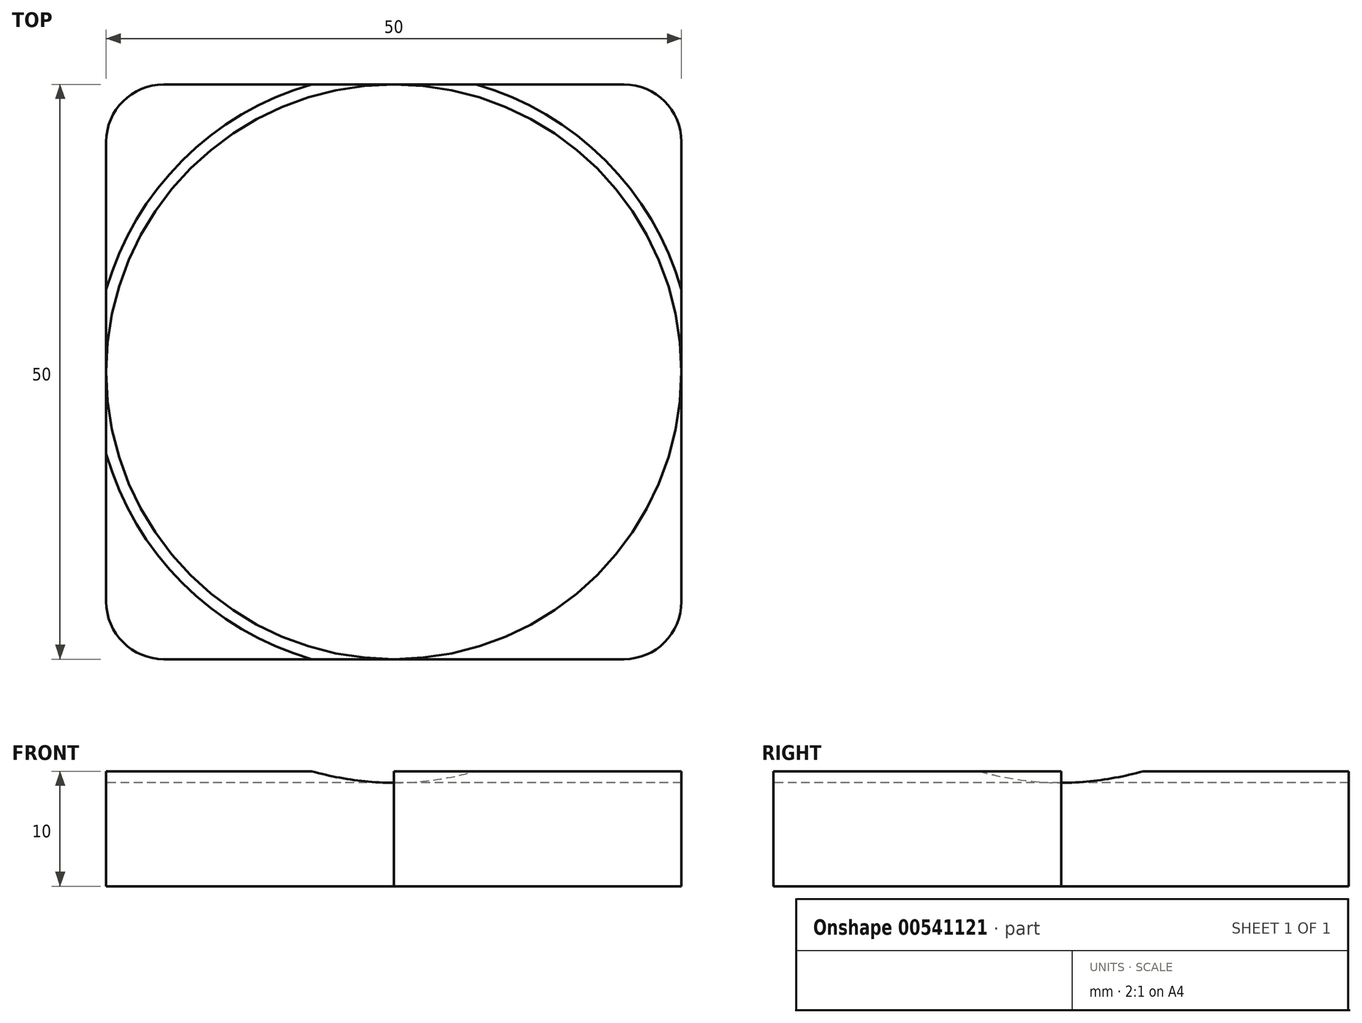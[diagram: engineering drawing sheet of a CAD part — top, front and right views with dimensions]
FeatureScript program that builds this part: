
annotation { "Feature Type Name" : "Feature", "Feature Type Description" : "" }
export const myFeature = defineFeature(function(context is Context, id is Id, definition is map)
    precondition{}
    {
        {
            var Q0;
            Q0=qCreatedBy(makeId("Top.planeOp"),FACE);
            var sketch = newSketch(context, id + "F0", { "sketchPlane" : qUnion([Q0])});
            skLineSegment(sketch, "E0.bottom", {"start": v(25, 25) * mm, "end": v(-25, 25) * mm});
            skLineSegment(sketch, "E0.top", {"start": v(25, -25) * mm, "end": v(-25, -25) * mm});
            skLineSegment(sketch, "E0.left", {"start": v(25, 25) * mm, "end": v(25, -25) * mm});
            skLineSegment(sketch, "E0.right", {"start": v(-25, 25) * mm, "end": v(-25, -25) * mm});
            skPoint(sketch, "E0.middle", {"position": v(0, 0) * mm});
            skSolve(sketch);
        }
        {
            var Q0;
            Q0=makeQuery(id+"F0.imprint","IMPRINT",FACE,{"disambiguationData":[TD([[makeQuery(id+"F0.imprint","IMPRINT",EDGE,{"derivedFrom":sQuery(id+"F0.wireOp",EDGE,"E0.bottom")}),1.0]])]});
            extrude(context, id + "F1", {"entities" : qUnion([Q0]), "depth" : 10 * mm, "offsetDistance" : 25 * mm});
        }
        {
            var Q0;
            Q0=makeQuery(id+"F1.opExtrude","CAP_FACE",FACE,{"disambiguationData":[OSD([sQuery(id+"F0.wireOp",EDGE,"E0.bottom"),sQuery(id+"F0.wireOp",EDGE,"E0.top"),sQuery(id+"F0.wireOp",EDGE,"E0.left"),sQuery(id+"F0.wireOp",EDGE,"E0.right")])],"isStart":false});
            var sketch = newSketch(context, id + "F2", { "sketchPlane" : qUnion([Q0])});
            skCircle(sketch, "E1", {"center": v(0, 0) * mm, "radius": 25 * mm});
            skSolve(sketch);
        }
        {
            var Q0;
            {var subQ0=sQuery(id+"F2.wireOp",EDGE,"E1");var subQ1=makeQuery(id+"F2.imprint","INTERSECT",VERTEX,{"derivedFrom":[makeQuery(id+"F1.opExtrude","CAP_EDGE",EDGE,{"disambiguationData":[OSD([sQuery(id+"F0.wireOp",EDGE,"E0.bottom")])],"isStart":false}),subQ0]});Q0=makeQuery(id+"F2.imprint","IMPRINT",FACE,{"disambiguationData":[TD([[makeQuery(id+"F2.imprint","IMPRINT",EDGE,{"disambiguationData":[TD([[subQ1,1.0]])],"derivedFrom":subQ0}),1.0]])]});}
            extrude(context, id + "F3", {"entities" : qUnion([Q0]), "operationType" : NewBodyOperationType.REMOVE, "endBound" : BoundingType.THROUGH_ALL, "oppositeDirection" : true, "depth" : 25 * mm, "offsetDistance" : 25 * mm});
        }
        {
            var Q0;
            Q0=makeQuery(id+"F1.opExtrude","SWEPT_EDGE",EDGE,{"disambiguationData":[OSD([sQuery(id+"F0.wireOp",EDGE,"E0.top"),sQuery(id+"F0.wireOp",EDGE,"E0.left")])]});
            var Q1;
            Q1=makeQuery(id+"F1.opExtrude","SWEPT_EDGE",EDGE,{"disambiguationData":[OSD([sQuery(id+"F0.wireOp",EDGE,"E0.bottom"),sQuery(id+"F0.wireOp",EDGE,"E0.left")])]});
            var Q2;
            Q2=makeQuery(id+"F1.opExtrude","SWEPT_EDGE",EDGE,{"disambiguationData":[OSD([sQuery(id+"F0.wireOp",EDGE,"E0.bottom"),sQuery(id+"F0.wireOp",EDGE,"E0.right")])]});
            var Q3;
            Q3=makeQuery(id+"F1.opExtrude","SWEPT_EDGE",EDGE,{"disambiguationData":[OSD([sQuery(id+"F0.wireOp",EDGE,"E0.top"),sQuery(id+"F0.wireOp",EDGE,"E0.right")])]});
            fillet(context, id + "F4", {"entities" : qUnion([Q0, Q1, Q2, Q3]), "radius" : 5 * mm, "tangentPropagation" : true, "allowEdgeOverflow" : false});
        }
        {
            var Q0;
            {var subQ0=sQuery(id+"F0.wireOp",EDGE,"E0.right");var subQ1=sQuery(id+"F0.wireOp",EDGE,"E0.top");var subQ2=sQuery(id+"F2.wireOp",EDGE,"E1");Q0=makeQuery(id+"F3.boolean.opBoolean","COPY",EDGE,{"disambiguationData":[TD([makeQuery(id+"F1.opExtrude","CAP_FACE",FACE,{"disambiguationData":[OSD([sQuery(id+"F0.wireOp",EDGE,"E0.bottom"),subQ1,sQuery(id+"F0.wireOp",EDGE,"E0.left"),subQ0])],"isStart":false}),makeQuery(id+"F1.opExtrude","SWEPT_FACE",FACE,{"disambiguationData":[OSD([subQ1])]}),makeQuery(id+"F1.opExtrude","SWEPT_FACE",FACE,{"disambiguationData":[OSD([subQ0])]}),makeQuery(id+"F3.opExtrude","SWEPT_FACE",FACE,{"disambiguationData":[OSD([subQ2])]})])],"derivedFrom":makeQuery(id+"F3.opExtrude","CAP_EDGE",EDGE,{"disambiguationData":[OSD([subQ2])],"isStart":true})});}
            var Q1;
            {var subQ0=sQuery(id+"F0.wireOp",EDGE,"E0.left");var subQ1=sQuery(id+"F0.wireOp",EDGE,"E0.top");var subQ2=sQuery(id+"F2.wireOp",EDGE,"E1");Q1=makeQuery(id+"F3.boolean.opBoolean","COPY",EDGE,{"disambiguationData":[TD([makeQuery(id+"F1.opExtrude","CAP_FACE",FACE,{"disambiguationData":[OSD([sQuery(id+"F0.wireOp",EDGE,"E0.bottom"),subQ1,subQ0,sQuery(id+"F0.wireOp",EDGE,"E0.right")])],"isStart":false}),makeQuery(id+"F1.opExtrude","SWEPT_FACE",FACE,{"disambiguationData":[OSD([subQ1])]}),makeQuery(id+"F1.opExtrude","SWEPT_FACE",FACE,{"disambiguationData":[OSD([subQ0])]}),makeQuery(id+"F3.opExtrude","SWEPT_FACE",FACE,{"disambiguationData":[OSD([subQ2])]})])],"derivedFrom":makeQuery(id+"F3.opExtrude","CAP_EDGE",EDGE,{"disambiguationData":[OSD([subQ2])],"isStart":true})});}
            var Q2;
            {var subQ0=sQuery(id+"F0.wireOp",EDGE,"E0.bottom");var subQ1=sQuery(id+"F0.wireOp",EDGE,"E0.left");var subQ2=sQuery(id+"F2.wireOp",EDGE,"E1");Q2=makeQuery(id+"F3.boolean.opBoolean","COPY",EDGE,{"disambiguationData":[TD([makeQuery(id+"F1.opExtrude","SWEPT_FACE",FACE,{"disambiguationData":[OSD([subQ0])]}),makeQuery(id+"F1.opExtrude","CAP_FACE",FACE,{"disambiguationData":[OSD([subQ0,sQuery(id+"F0.wireOp",EDGE,"E0.top"),subQ1,sQuery(id+"F0.wireOp",EDGE,"E0.right")])],"isStart":false}),makeQuery(id+"F1.opExtrude","SWEPT_FACE",FACE,{"disambiguationData":[OSD([subQ1])]}),makeQuery(id+"F3.opExtrude","SWEPT_FACE",FACE,{"disambiguationData":[OSD([subQ2])]})])],"derivedFrom":makeQuery(id+"F3.opExtrude","CAP_EDGE",EDGE,{"disambiguationData":[OSD([subQ2])],"isStart":true})});}
            var Q3;
            {var subQ0=sQuery(id+"F0.wireOp",EDGE,"E0.bottom");var subQ1=sQuery(id+"F0.wireOp",EDGE,"E0.right");var subQ2=sQuery(id+"F2.wireOp",EDGE,"E1");Q3=makeQuery(id+"F3.boolean.opBoolean","COPY",EDGE,{"disambiguationData":[TD([makeQuery(id+"F1.opExtrude","SWEPT_FACE",FACE,{"disambiguationData":[OSD([subQ0])]}),makeQuery(id+"F1.opExtrude","CAP_FACE",FACE,{"disambiguationData":[OSD([subQ0,sQuery(id+"F0.wireOp",EDGE,"E0.top"),sQuery(id+"F0.wireOp",EDGE,"E0.left"),subQ1])],"isStart":false}),makeQuery(id+"F1.opExtrude","SWEPT_FACE",FACE,{"disambiguationData":[OSD([subQ1])]}),makeQuery(id+"F3.opExtrude","SWEPT_FACE",FACE,{"disambiguationData":[OSD([subQ2])]})])],"derivedFrom":makeQuery(id+"F3.opExtrude","CAP_EDGE",EDGE,{"disambiguationData":[OSD([subQ2])],"isStart":true})});}
            chamfer(context, id + "F5", {"entities" : qUnion([Q0, Q1, Q2, Q3]), "chamferType" : ChamferType.OFFSET_ANGLE, "width" : 1 * mm, "oppositeDirection" : false, "angle" : 45 * degree, "tangentPropagation" : true});
        }
    });
